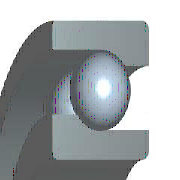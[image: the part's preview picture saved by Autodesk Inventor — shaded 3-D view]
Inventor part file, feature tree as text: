
AUTODESK INVENTOR PART (.ipt)
format: ipt  version: 2018 (Build 220112000, 112)  size: 308,736 bytes
history: native  units: mm (DEFAULTED — no unit token found)
features: other x5, plane x3, sketch x1, pattern_circular x1
ambient origin geometry x8: Origin, YZ Plane, XZ Plane, XY Plane, X Axis, Y Axis, Z Axis, Center Point
bodies: Solid1 (feature_tree)
feature tree (10):
  plane  "WorkPlane1"
  plane  "Work Plane2"
  plane  "WorkPlane2"
  other  "WorkPoint1"
  other  "WorkPoint3"
  other  "WorkPoint2"
  other  "WorkAxis1"
  sketch  "Schizzo7"
  other  "Work Axis2"
  pattern_circular  "Seriepolare1"  [2 undecoded]
note: 2 required parameter values undecoded (feature->parameter linkage not recoverable at this tier; creation-order binding heuristic only, values carry confidence <= 0.55)
